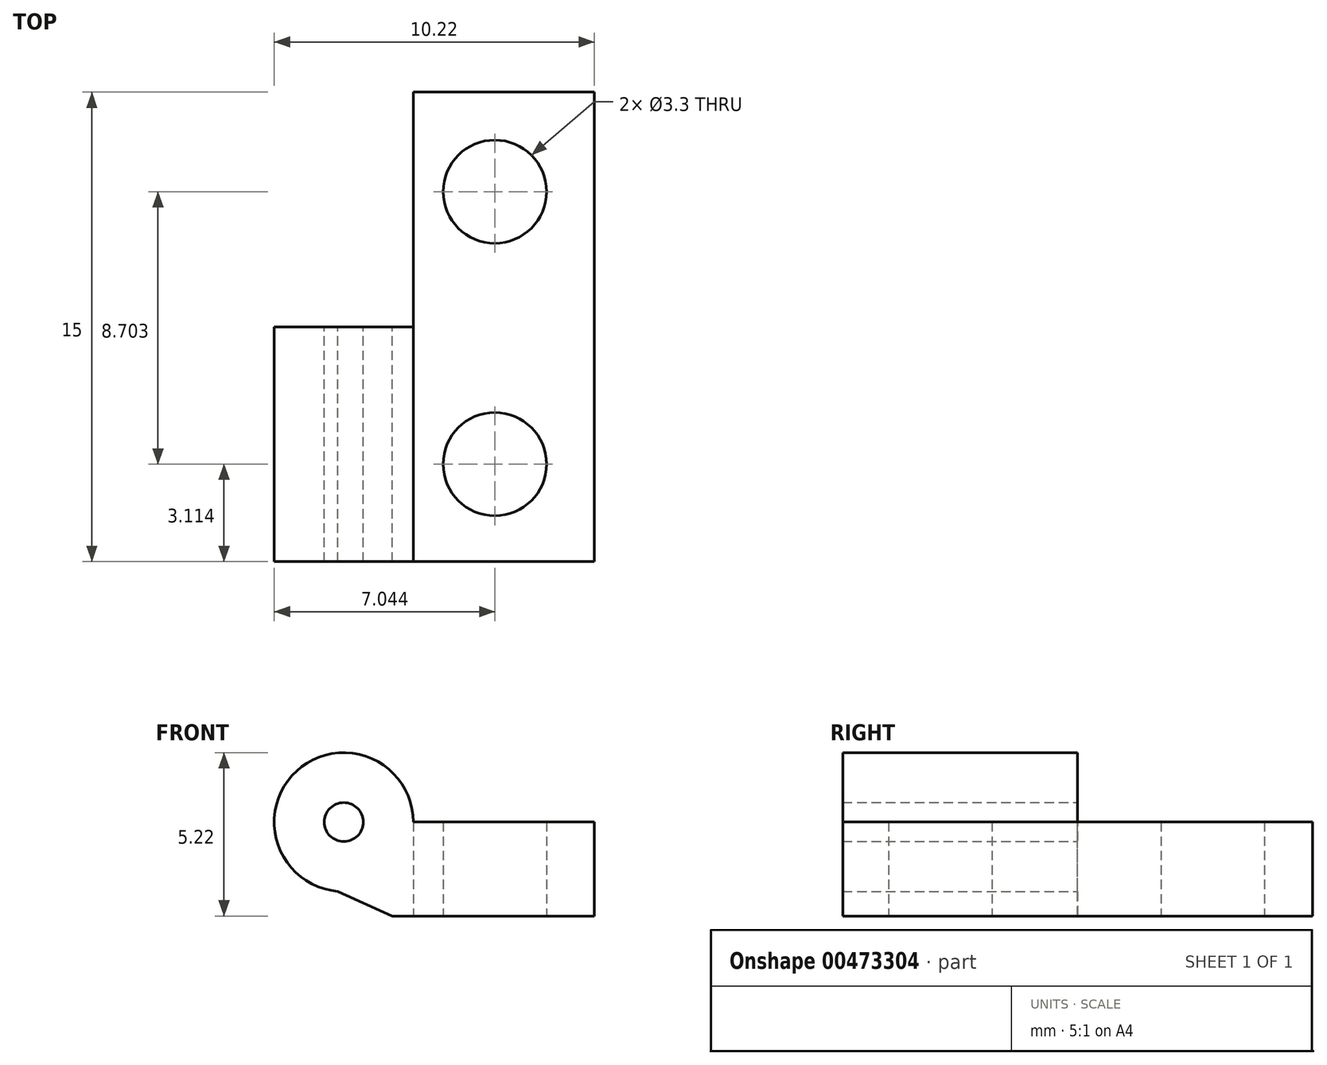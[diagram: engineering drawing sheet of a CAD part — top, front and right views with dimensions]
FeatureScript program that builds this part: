
annotation { "Feature Type Name" : "Feature", "Feature Type Description" : "" }
export const myFeature = defineFeature(function(context is Context, id is Id, definition is map)
    precondition{}
    {
        {
            var Q0;
            Q0=qCreatedBy(makeId("Top.planeOp"),FACE);
            var sketch = newSketch(context, id + "F0", { "sketchPlane" : qUnion([Q0])});
            skLineSegment(sketch, "E0.bottom", {"start": v(0, 0) * mm, "end": v(16, 0) * mm});
            skLineSegment(sketch, "E0.top", {"start": v(0, 15) * mm, "end": v(16, 15) * mm});
            skLineSegment(sketch, "E0.left", {"start": v(0, 0) * mm, "end": v(0, 15) * mm});
            skLineSegment(sketch, "E0.right", {"start": v(16, 0) * mm, "end": v(16, 15) * mm});
            skCircle(sketch, "E1", {"center": v(3.1, 11.82) * mm, "radius": 1.65 * mm});
            skCircle(sketch, "E2", {"center": v(12.82, 11.82) * mm, "radius": 1.65 * mm});
            skCircle(sketch, "E3", {"center": v(3.1, 3.11) * mm, "radius": 1.65 * mm});
            skCircle(sketch, "E4", {"center": v(12.82, 3.11) * mm, "radius": 1.65 * mm});
            skSolve(sketch);
        }
        {
            var Q0;
            Q0 = qSketchRegion(id + "F0", true);
            extrude(context, id + "F1", {"entities" : qUnion([Q0]), "depth" : 3 * mm, "offsetDistance" : 25 * mm});
        }
        {
            var Q0;
            Q0=makeQuery(id+"F1.opExtrude","SWEPT_FACE",FACE,{"disambiguationData":[OSD([sQuery(id+"F0.wireOp",EDGE,"E0.top")])]});
            var sketch = newSketch(context, id + "F2", { "sketchPlane" : qUnion([Q0])});
            skCircle(sketch, "E5", {"center": v(-8, 3) * mm, "radius": 2.22 * mm});
            skSolve(sketch);
        }
        {
            var Q0;
            Q0 = qSketchRegion(id + "F2", true);
            var Q1;
            Q1=makeQuery(id+"F1.opExtrude","SWEPT_FACE",FACE,{"disambiguationData":[OSD([sQuery(id+"F0.wireOp",EDGE,"E0.bottom")])]});
            extrude(context, id + "F3", {"entities" : qUnion([Q0]), "operationType" : NewBodyOperationType.ADD, "endBound" : BoundingType.UP_TO_SURFACE, "oppositeDirection" : true, "depth" : 25 * mm, "endBoundEntityFace" : qUnion([Q1]), "offsetDistance" : 25 * mm});
        }
        {
            var Q0;
            Q0=makeQuery(id+"F3.boolean.opBoolean","MERGE",FACE,{"derivedFrom":[makeQuery(id+"F1.opExtrude","SWEPT_FACE",FACE,{"disambiguationData":[OSD([sQuery(id+"F0.wireOp",EDGE,"E0.top")])]}),makeQuery(id+"F3.opExtrude","CAP_FACE",FACE,{"disambiguationData":[OSD([sQuery(id+"F2.wireOp",EDGE,"E5")])],"isStart":true})]});
            var sketch = newSketch(context, id + "F4", { "sketchPlane" : qUnion([Q0])});
            skCircle(sketch, "E6", {"center": v(-8, 3) * mm, "radius": 0.62 * mm});
            skLineSegment(sketch, "E7", {"start": v(-9.55, 0) * mm, "end": v(-8, 0.9) * mm});
            skLineSegment(sketch, "E8", {"start": v(-8, 0.9) * mm, "end": v(-6.45, 0) * mm});
            skLineSegment(sketch, "E9", {"start": v(-9.55, 0) * mm, "end": v(-6.45, 0) * mm});
            skSolve(sketch);
        }
        {
            var Q0;
            Q0 = qSketchRegion(id + "F4", true);
            extrude(context, id + "F5", {"entities" : qUnion([Q0]), "operationType" : NewBodyOperationType.REMOVE, "oppositeDirection" : true, "depth" : 25 * mm, "offsetDistance" : 25 * mm});
        }
        {
            var Q0;
            Q0=makeQuery(id+"F3.boolean.opBoolean","MERGE",FACE,{"derivedFrom":[makeQuery(id+"F1.opExtrude","SWEPT_FACE",FACE,{"disambiguationData":[OSD([sQuery(id+"F0.wireOp",EDGE,"E0.top")])]}),makeQuery(id+"F3.opExtrude","CAP_FACE",FACE,{"disambiguationData":[OSD([sQuery(id+"F2.wireOp",EDGE,"E5")])],"isStart":true})]});
            var sketch = newSketch(context, id + "F6", { "sketchPlane" : qUnion([Q0])});
            skArc(sketch, "E10", {"start": v(-8.19, 0.79) * mm, "mid": v(-6.5, 1.37) * mm, "end": v(-5.78, 3) * mm});
            skLineSegment(sketch, "E11", {"start": v(-9.55, 0) * mm, "end": v(-8.19, 0.79) * mm});
            skLineSegment(sketch, "E12", {"start": v(-5.78, 3) * mm, "end": v(0, 3) * mm});
            skLineSegment(sketch, "E13", {"start": v(0, 3) * mm, "end": v(0, -1.07) * mm});
            skLineSegment(sketch, "E14", {"start": v(0, -1.07) * mm, "end": v(-9.55, 0) * mm});
            skSolve(sketch);
        }
        {
            var Q0;
            Q0 = qSketchRegion(id + "F6", true);
            extrude(context, id + "F7", {"entities" : qUnion([Q0]), "operationType" : NewBodyOperationType.REMOVE, "oppositeDirection" : true, "depth" : 25 * mm, "offsetDistance" : 25 * mm});
        }
        {
            var Q0;
            Q0=makeQuery(id+"F3.boolean.opBoolean","MERGE",FACE,{"derivedFrom":[makeQuery(id+"F1.opExtrude","SWEPT_FACE",FACE,{"disambiguationData":[OSD([sQuery(id+"F0.wireOp",EDGE,"E0.top")])]}),makeQuery(id+"F3.opExtrude","CAP_FACE",FACE,{"disambiguationData":[OSD([sQuery(id+"F2.wireOp",EDGE,"E5")])],"isStart":true})]});
            var sketch = newSketch(context, id + "F8", { "sketchPlane" : qUnion([Q0])});
            skLineSegment(sketch, "E15", {"start": v(-9.55, 0) * mm, "end": v(-7.81, 0.79) * mm});
            skLineSegment(sketch, "E16", {"start": v(-7.81, 0.79) * mm, "end": v(-8, 0.9) * mm});
            skLineSegment(sketch, "E17", {"start": v(-8, 0.9) * mm, "end": v(-9.55, 0) * mm});
            skSolve(sketch);
        }
        {
            var Q0;
            Q0 = qSketchRegion(id + "F8", true);
            var Q1;
            {var subQ0=sQuery(id+"F0.wireOp",EDGE,"E0.bottom");Q1=makeQuery(id+"F3.boolean.opBoolean","MERGE",FACE,{"derivedFrom":[makeQuery(id+"F1.opExtrude","SWEPT_FACE",FACE,{"disambiguationData":[OSD([subQ0])]}),makeQuery(id+"F3.opExtrude","CAP_FACE",FACE,{"disambiguationData":[OSD([subQ0])],"isStart":false})]});}
            extrude(context, id + "F9", {"entities" : qUnion([Q0]), "operationType" : NewBodyOperationType.ADD, "endBound" : BoundingType.UP_TO_SURFACE, "oppositeDirection" : true, "depth" : 25 * mm, "endBoundEntityFace" : qUnion([Q1]), "offsetDistance" : 25 * mm});
        }
        {
            var Q0;
            {var subQ0=sQuery(id+"F0.wireOp",EDGE,"E2");var subQ1=sQuery(id+"F0.wireOp",EDGE,"E0.top");var subQ3=sQuery(id+"F0.wireOp",EDGE,"E0.right");var subQ4=sQuery(id+"F0.wireOp",EDGE,"E0.bottom");var subQ5=sQuery(id+"F0.wireOp",EDGE,"E4");Q0=makeQuery(id+"F3.boolean.opBoolean","SPLIT",FACE,{"disambiguationData":[TD([makeQuery(id+"F1.opExtrude","SWEPT_FACE",FACE,{"disambiguationData":[OSD([subQ3])]})])],"derivedFrom":makeQuery(id+"F1.opExtrude","CAP_FACE",FACE,{"disambiguationData":[OSD([subQ4,subQ1,sQuery(id+"F0.wireOp",EDGE,"E0.left"),subQ3,sQuery(id+"F0.wireOp",EDGE,"E1"),subQ0,sQuery(id+"F0.wireOp",EDGE,"E3"),subQ5])],"isStart":false})});}
            var sketch = newSketch(context, id + "F10", { "sketchPlane" : qUnion([Q0])});
            skLineSegment(sketch, "E18.bottom", {"start": v(10.22, 7.5) * mm, "end": v(2.43, 7.5) * mm});
            skLineSegment(sketch, "E18.top", {"start": v(10.22, 16.15) * mm, "end": v(2.43, 16.15) * mm});
            skLineSegment(sketch, "E18.left", {"start": v(10.22, 7.5) * mm, "end": v(10.22, 16.15) * mm});
            skLineSegment(sketch, "E18.right", {"start": v(2.43, 7.5) * mm, "end": v(2.43, 16.15) * mm});
            skSolve(sketch);
        }
        {
            var Q0;
            Q0 = qSketchRegion(id + "F10", true);
            extrude(context, id + "F11", {"entities" : qUnion([Q0]), "operationType" : NewBodyOperationType.REMOVE, "oppositeDirection" : true, "depth" : 25 * mm, "offsetDistance" : 25 * mm, "hasSecondDirection" : true, "secondDirectionOppositeDirection" : false, "secondDirectionDepth" : 25 * mm});
        }
    });
